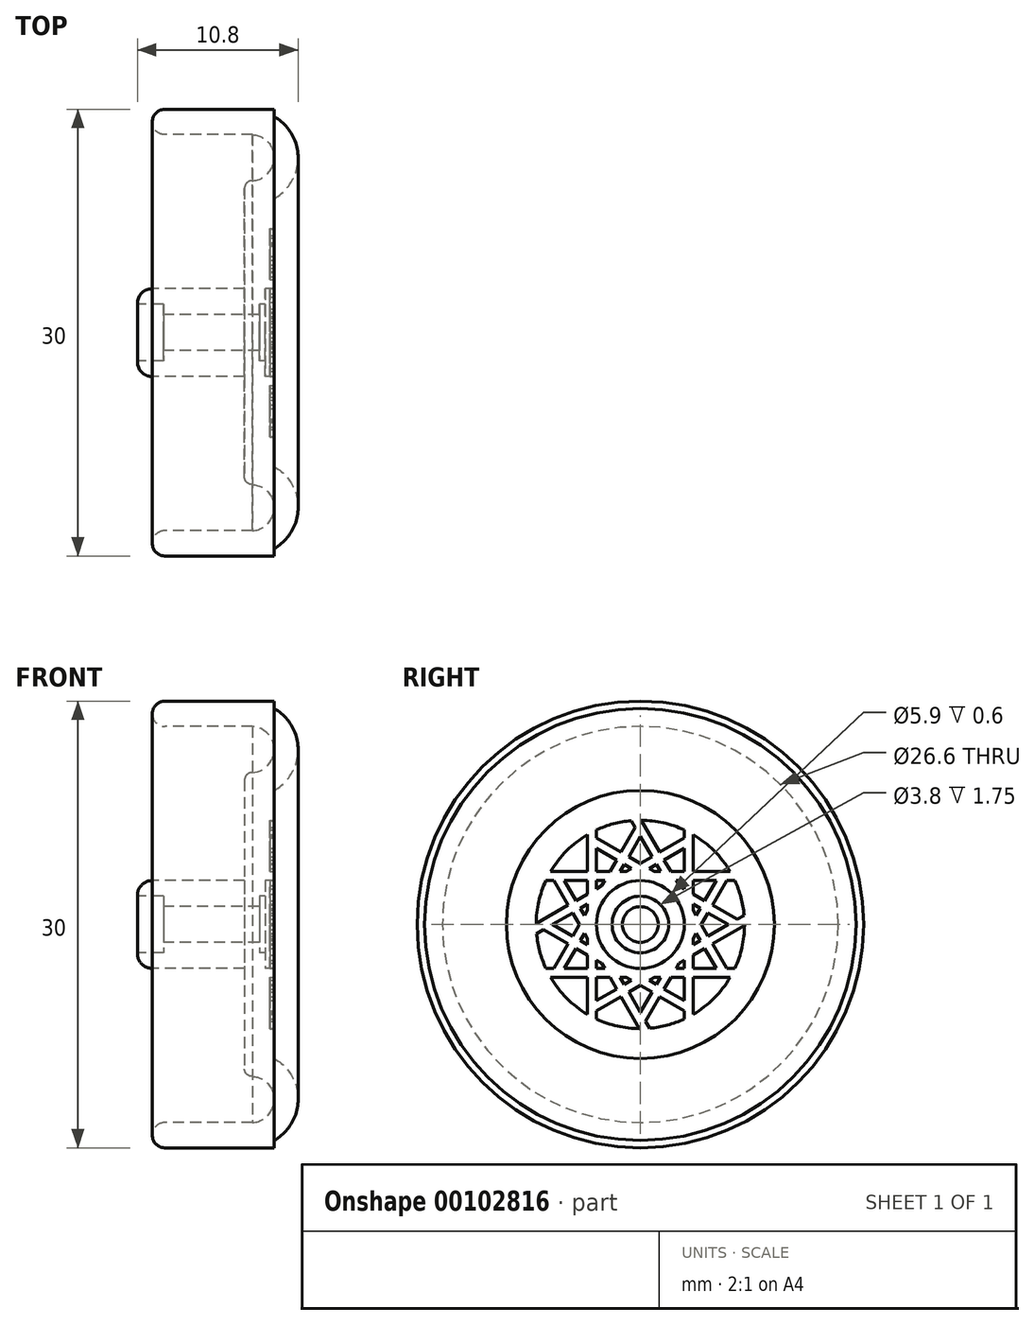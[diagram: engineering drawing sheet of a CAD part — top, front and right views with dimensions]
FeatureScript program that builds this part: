
annotation { "Feature Type Name" : "Feature", "Feature Type Description" : "" }
export const myFeature = defineFeature(function(context is Context, id is Id, definition is map)
    precondition{}
    {
        {
            var Q0;
            Q0=qCreatedBy(makeId("Top.planeOp"),FACE);
            var sketch = newSketch(context, id + "F0", { "sketchPlane" : qUnion([Q0])});
            skLineSegment(sketch, "E0.bottom", {"start": v(4.9, 15) * mm, "end": v(-4.9, 15) * mm, "construction": true});
            skLineSegment(sketch, "E0.top", {"start": v(4.9, -15) * mm, "end": v(-4.9, -15) * mm, "construction": true});
            skLineSegment(sketch, "E0.left", {"start": v(4.9, 15) * mm, "end": v(4.9, -15) * mm, "construction": true});
            skPoint(sketch, "E0.middle", {"position": v(0, 0) * mm});
            skLineSegment(sketch, "E1", {"start": v(-4.05, 15) * mm, "end": v(3.3, 15) * mm});
            skLineSegment(sketch, "E2", {"start": v(3.3, 9) * mm, "end": v(3.3, 2.95) * mm});
            skLineSegment(sketch, "E3", {"start": v(2.3, 1.2) * mm, "end": v(-4.15, 1.2) * mm});
            skLineSegment(sketch, "E4", {"start": v(-4.15, 1.2) * mm, "end": v(-4.15, 1.9) * mm});
            skLineSegment(sketch, "E5", {"start": v(-4.15, 1.9) * mm, "end": v(-5.9, 1.9) * mm});
            skLineSegment(sketch, "E6.0", {"start": v(-4.05, 13.3) * mm, "end": v(1.84, 13.3) * mm});
            skLineSegment(sketch, "E7.0", {"start": v(1.3, 9.7) * mm, "end": v(1.3, 2.95) * mm});
            skLineSegment(sketch, "E8.0", {"start": v(1.3, 2.95) * mm, "end": v(-4.9, 2.95) * mm});
            skArc(sketch, "E9", {"start": v(-4.05, 15) * mm, "mid": v(-4.9, 14.15) * mm, "end": v(-4.05, 13.3) * mm});
            skLineSegment(sketch, "E10", {"start": v(2.3, 1.2) * mm, "end": v(2.3, 1.9) * mm});
            skLineSegment(sketch, "E11", {"start": v(2.3, 1.9) * mm, "end": v(2.7, 1.9) * mm});
            skLineSegment(sketch, "E12", {"start": v(2.7, 1.9) * mm, "end": v(2.7, 2.95) * mm});
            skLineSegment(sketch, "E13", {"start": v(2.7, 2.95) * mm, "end": v(3.3, 2.95) * mm});
            skLineSegment(sketch, "E14", {"start": v(-5.9, 1.95) * mm, "end": v(-5.9, 1.9) * mm});
            skLineSegment(sketch, "E15", {"start": v(-5, 0) * mm, "end": v(4.9, 0) * mm, "construction": true});
            skPoint(sketch, "E16.visualSharp", {"position": v(-5.9, 2.95) * mm});
            skArc(sketch, "E16.filletArc", {"start": v(-4.9, 2.95) * mm, "mid": v(-5.6, 2.66) * mm, "end": v(-5.9, 1.95) * mm});
            skLineSegment(sketch, "E17", {"start": v(1.23, 0) * mm, "end": v(1.23, 17.38) * mm, "construction": true});
            skLineSegment(sketch, "E18", {"start": v(3.3, 15) * mm, "end": v(3.3, 14.5) * mm});
            skArc(sketch, "E19", {"start": v(3.3, 9) * mm, "mid": v(4.9, 11.75) * mm, "end": v(3.3, 14.5) * mm});
            skLineSegment(sketch, "E20", {"start": v(-4.9, 15) * mm, "end": v(-4.9, 12.83) * mm, "construction": true});
            skArc(sketch, "E21", {"start": v(1.78, 10.2) * mm, "mid": v(3.29, 11.72) * mm, "end": v(1.84, 13.3) * mm});
            skPoint(sketch, "E22.visualSharp", {"position": v(1.3, 10.26) * mm});
            skArc(sketch, "E22.filletArc", {"start": v(1.78, 10.2) * mm, "mid": v(1.44, 10.05) * mm, "end": v(1.3, 9.7) * mm});
            skSolve(sketch);
        }
        {
            var Q0;
            Q0=makeQuery(id+"F0.imprint","IMPRINT",FACE,{"disambiguationData":[TD([[makeQuery(id+"F0.imprint","IMPRINT",EDGE,{"derivedFrom":sQuery(id+"F0.wireOp",EDGE,"E1")}),-1.0]])]});
            var Q1;
            Q1=sQuery(id+"F0.wireOp",EDGE,"E15");
            revolve(context, id + "F1", {"entities" : qUnion([Q0]), "axis" : qUnion([Q1]), "revolveType" : RevolveType.FULL});
        }
        {
            var Q0;
            Q0=makeQuery(id+"F1.opRevolve","SWEPT_FACE",FACE,{"disambiguationData":[OSD([sQuery(id+"F0.wireOp",EDGE,"E2")])]});
            var sketch = newSketch(context, id + "F2", { "sketchPlane" : qUnion([Q0])});
            skCircle(sketch, "E23", {"center": v(0, 0) * mm, "radius": 7 * mm});
            skLineSegment(sketch, "E24", {"start": v(2.95, 6.35) * mm, "end": v(2.95, -6.35) * mm});
            skLineSegment(sketch, "E25.0", {"start": v(3.55, 6.03) * mm, "end": v(3.55, -6.03) * mm});
            skLineSegment(sketch, "E26.1.0", {"start": v(-3.55, -6.03) * mm, "end": v(-3.55, 6.03) * mm});
            skLineSegment(sketch, "E26.1.1", {"start": v(-2.95, -6.35) * mm, "end": v(-2.95, 6.35) * mm});
            skLineSegment(sketch, "E27.1.0", {"start": v(6.35, -2.95) * mm, "end": v(-6.35, -2.95) * mm});
            skLineSegment(sketch, "E27.1.1", {"start": v(6.03, -3.55) * mm, "end": v(-6.03, -3.55) * mm});
            skLineSegment(sketch, "E27.1.2", {"start": v(-6.03, 3.55) * mm, "end": v(6.03, 3.55) * mm});
            skLineSegment(sketch, "E27.1.3", {"start": v(-6.35, 2.95) * mm, "end": v(6.35, 2.95) * mm});
            skLineSegment(sketch, "E28.1.0", {"start": v(6.97, 0.62) * mm, "end": v(-4.02, -5.73) * mm});
            skLineSegment(sketch, "E28.1.1", {"start": v(7, -0.06) * mm, "end": v(-3.45, -6.1) * mm});
            skLineSegment(sketch, "E28.1.2", {"start": v(-0.06, -7) * mm, "end": v(-6.1, 3.45) * mm});
            skLineSegment(sketch, "E28.1.3", {"start": v(0.62, -6.97) * mm, "end": v(-5.73, 4.02) * mm});
            skLineSegment(sketch, "E28.1.4", {"start": v(-0.62, 6.97) * mm, "end": v(5.73, -4.02) * mm});
            skLineSegment(sketch, "E28.1.5", {"start": v(0.06, 7) * mm, "end": v(6.1, -3.45) * mm});
            skLineSegment(sketch, "E28.1.6", {"start": v(-6.97, -0.62) * mm, "end": v(4.02, 5.73) * mm});
            skLineSegment(sketch, "E28.1.7", {"start": v(-7, 0.06) * mm, "end": v(3.45, 6.1) * mm});
            skLineSegment(sketch, "E28.2.0", {"start": v(-4.02, 5.73) * mm, "end": v(6.97, -0.62) * mm});
            skLineSegment(sketch, "E28.2.1", {"start": v(-3.45, 6.1) * mm, "end": v(7, 0.06) * mm});
            skLineSegment(sketch, "E28.2.2", {"start": v(6.1, 3.45) * mm, "end": v(0.06, -7) * mm});
            skLineSegment(sketch, "E28.2.3", {"start": v(5.73, 4.02) * mm, "end": v(-0.62, -6.97) * mm});
            skLineSegment(sketch, "E28.2.4", {"start": v(-5.73, -4.02) * mm, "end": v(0.62, 6.97) * mm});
            skLineSegment(sketch, "E28.2.5", {"start": v(-6.1, -3.45) * mm, "end": v(-0.06, 7) * mm});
            skLineSegment(sketch, "E28.2.6", {"start": v(4.02, -5.73) * mm, "end": v(-6.97, 0.62) * mm});
            skLineSegment(sketch, "E28.2.7", {"start": v(3.45, -6.1) * mm, "end": v(-7, -0.06) * mm});
            skSolve(sketch);
        }
        {
            var Q0;
            {var subQ0=sQuery(id+"F2.wireOp",EDGE,"E28.1.3");var subQ1=sQuery(id+"F2.wireOp",EDGE,"E23");var subQ2=makeQuery(id+"F2.imprint","INTERSECT",VERTEX,{"disambiguationData":[OD(1.0)],"derivedFrom":[subQ1,subQ0]});Q0=makeQuery(id+"F2.imprint","IMPRINT",FACE,{"disambiguationData":[TD([[makeQuery(id+"F2.imprint","IMPRINT",EDGE,{"disambiguationData":[TD([[subQ2,1.0]])],"derivedFrom":subQ1}),1.0]])]});}
            var Q1;
            {var subQ0=sQuery(id+"F2.wireOp",EDGE,"E26.1.0");var subQ1=sQuery(id+"F2.wireOp",EDGE,"E23");var subQ2=makeQuery(id+"F2.imprint","INTERSECT",VERTEX,{"disambiguationData":[OD(1.0)],"derivedFrom":[subQ1,subQ0]});Q1=makeQuery(id+"F2.imprint","IMPRINT",FACE,{"disambiguationData":[TD([[makeQuery(id+"F2.imprint","IMPRINT",EDGE,{"disambiguationData":[TD([[subQ2,-1.0]])],"derivedFrom":subQ1}),1.0]])]});}
            var Q2;
            {var subQ0=sQuery(id+"F2.wireOp",EDGE,"E27.1.2");var subQ1=sQuery(id+"F2.wireOp",EDGE,"E26.1.1");var subQ2=makeQuery(id+"F2.imprint","INTERSECT",VERTEX,{"derivedFrom":[subQ1,subQ0]});Q2=makeQuery(id+"F2.imprint","IMPRINT",FACE,{"disambiguationData":[TD([[makeQuery(id+"F2.imprint","IMPRINT",EDGE,{"disambiguationData":[TD([[subQ2,-1.0]])],"derivedFrom":subQ1}),-1.0]])]});}
            var Q3;
            {var subQ1=sQuery(id+"F2.wireOp",EDGE,"E23");var subQ5=sQuery(id+"F2.wireOp",EDGE,"E26.1.1");var subQ6=makeQuery(id+"F2.imprint","INTERSECT",VERTEX,{"disambiguationData":[OD(1.0)],"derivedFrom":[subQ1,subQ5]});Q3=makeQuery(id+"F2.imprint","IMPRINT",FACE,{"disambiguationData":[TD([[makeQuery(id+"F2.imprint","IMPRINT",EDGE,{"disambiguationData":[TD([[subQ6,1.0]])],"derivedFrom":subQ1}),1.0]])]});}
            var Q4;
            {var subQ0=sQuery(id+"F2.wireOp",EDGE,"E28.1.5");var subQ1=sQuery(id+"F2.wireOp",EDGE,"E23");var subQ2=makeQuery(id+"F2.imprint","INTERSECT",VERTEX,{"disambiguationData":[OD(0.0)],"derivedFrom":[subQ1,subQ0]});Q4=makeQuery(id+"F2.imprint","IMPRINT",FACE,{"disambiguationData":[TD([[makeQuery(id+"F2.imprint","IMPRINT",EDGE,{"disambiguationData":[TD([[subQ2,1.0]])],"derivedFrom":subQ1}),1.0]])]});}
            var Q5;
            {var subQ1=sQuery(id+"F2.wireOp",EDGE,"E24");var subQ7=sQuery(id+"F2.wireOp",EDGE,"E23");var subQ8=makeQuery(id+"F2.imprint","INTERSECT",VERTEX,{"disambiguationData":[OD(0.0)],"derivedFrom":[subQ7,subQ1]});Q5=makeQuery(id+"F2.imprint","IMPRINT",FACE,{"disambiguationData":[TD([[makeQuery(id+"F2.imprint","IMPRINT",EDGE,{"disambiguationData":[TD([[subQ8,-1.0]])],"derivedFrom":subQ7}),1.0]])]});}
            var Q6;
            {var subQ0=sQuery(id+"F2.wireOp",EDGE,"E28.2.4");var subQ1=sQuery(id+"F2.wireOp",EDGE,"E28.1.4");var subQ2=makeQuery(id+"F2.imprint","INTERSECT",VERTEX,{"derivedFrom":[subQ1,subQ0]});Q6=makeQuery(id+"F2.imprint","IMPRINT",FACE,{"disambiguationData":[TD([[makeQuery(id+"F2.imprint","IMPRINT",EDGE,{"disambiguationData":[TD([[subQ2,-1.0]])],"derivedFrom":subQ1}),-1.0]])]});}
            var Q7;
            {var subQ0=sQuery(id+"F2.wireOp",EDGE,"E28.2.4");var subQ1=sQuery(id+"F2.wireOp",EDGE,"E27.1.2");var subQ2=makeQuery(id+"F2.imprint","INTERSECT",VERTEX,{"derivedFrom":[subQ1,subQ0]});Q7=makeQuery(id+"F2.imprint","IMPRINT",FACE,{"disambiguationData":[TD([[makeQuery(id+"F2.imprint","IMPRINT",EDGE,{"disambiguationData":[TD([[subQ2,-1.0]])],"derivedFrom":subQ1}),1.0]])]});}
            var Q8;
            {var subQ0=sQuery(id+"F2.wireOp",EDGE,"E28.2.1");var subQ1=sQuery(id+"F2.wireOp",EDGE,"E27.1.2");var subQ2=makeQuery(id+"F2.imprint","INTERSECT",VERTEX,{"derivedFrom":[subQ1,subQ0]});Q8=makeQuery(id+"F2.imprint","IMPRINT",FACE,{"disambiguationData":[TD([[makeQuery(id+"F2.imprint","IMPRINT",EDGE,{"disambiguationData":[TD([[subQ2,-1.0]])],"derivedFrom":subQ1}),1.0]])]});}
            var Q9;
            {var subQ0=sQuery(id+"F2.wireOp",EDGE,"E28.1.6");var subQ1=sQuery(id+"F2.wireOp",EDGE,"E24");var subQ2=makeQuery(id+"F2.imprint","INTERSECT",VERTEX,{"derivedFrom":[subQ1,subQ0]});Q9=makeQuery(id+"F2.imprint","IMPRINT",FACE,{"disambiguationData":[TD([[makeQuery(id+"F2.imprint","IMPRINT",EDGE,{"disambiguationData":[TD([[subQ2,-1.0]])],"derivedFrom":subQ1}),-1.0]])]});}
            var Q10;
            {var subQ0=sQuery(id+"F2.wireOp",EDGE,"E28.1.6");var subQ1=sQuery(id+"F2.wireOp",EDGE,"E23");var subQ2=makeQuery(id+"F2.imprint","INTERSECT",VERTEX,{"disambiguationData":[OD(1.0)],"derivedFrom":[subQ1,subQ0]});Q10=makeQuery(id+"F2.imprint","IMPRINT",FACE,{"disambiguationData":[TD([[makeQuery(id+"F2.imprint","IMPRINT",EDGE,{"disambiguationData":[TD([[subQ2,1.0]])],"derivedFrom":subQ1}),1.0]])]});}
            var Q11;
            {var subQ0=sQuery(id+"F2.wireOp",EDGE,"E27.1.3");var subQ1=sQuery(id+"F2.wireOp",EDGE,"E24");var subQ2=makeQuery(id+"F2.imprint","INTERSECT",VERTEX,{"derivedFrom":[subQ1,subQ0]});Q11=makeQuery(id+"F2.imprint","IMPRINT",FACE,{"disambiguationData":[TD([[makeQuery(id+"F2.imprint","IMPRINT",EDGE,{"disambiguationData":[TD([[subQ2,-1.0]])],"derivedFrom":subQ1}),-1.0]])]});}
            var Q12;
            {var subQ0=sQuery(id+"F2.wireOp",EDGE,"E27.1.3");var subQ1=sQuery(id+"F2.wireOp",EDGE,"E25.0");var subQ2=makeQuery(id+"F2.imprint","INTERSECT",VERTEX,{"derivedFrom":[subQ1,subQ0]});Q12=makeQuery(id+"F2.imprint","IMPRINT",FACE,{"disambiguationData":[TD([[makeQuery(id+"F2.imprint","IMPRINT",EDGE,{"disambiguationData":[TD([[subQ2,-1.0]])],"derivedFrom":subQ1}),1.0]])]});}
            var Q13;
            {var subQ5=sQuery(id+"F2.wireOp",EDGE,"E27.1.3");var subQ6=sQuery(id+"F2.wireOp",EDGE,"E23");var subQ7=makeQuery(id+"F2.imprint","INTERSECT",VERTEX,{"disambiguationData":[OD(1.0)],"derivedFrom":[subQ6,subQ5]});Q13=makeQuery(id+"F2.imprint","IMPRINT",FACE,{"disambiguationData":[TD([[makeQuery(id+"F2.imprint","IMPRINT",EDGE,{"disambiguationData":[TD([[subQ7,1.0]])],"derivedFrom":subQ6}),1.0]])]});}
            var Q14;
            {var subQ0=sQuery(id+"F2.wireOp",EDGE,"E28.2.0");var subQ1=sQuery(id+"F2.wireOp",EDGE,"E25.0");var subQ2=makeQuery(id+"F2.imprint","INTERSECT",VERTEX,{"derivedFrom":[subQ1,subQ0]});Q14=makeQuery(id+"F2.imprint","IMPRINT",FACE,{"disambiguationData":[TD([[makeQuery(id+"F2.imprint","IMPRINT",EDGE,{"disambiguationData":[TD([[subQ2,-1.0]])],"derivedFrom":subQ1}),1.0]])]});}
            var Q15;
            {var subQ0=sQuery(id+"F2.wireOp",EDGE,"E28.2.0");var subQ1=sQuery(id+"F2.wireOp",EDGE,"E28.1.0");var subQ2=makeQuery(id+"F2.imprint","INTERSECT",VERTEX,{"derivedFrom":[subQ1,subQ0]});Q15=makeQuery(id+"F2.imprint","IMPRINT",FACE,{"disambiguationData":[TD([[makeQuery(id+"F2.imprint","IMPRINT",EDGE,{"disambiguationData":[TD([[subQ2,-1.0]])],"derivedFrom":subQ1}),-1.0]])]});}
            var Q16;
            {var subQ5=sQuery(id+"F2.wireOp",EDGE,"E27.1.0");var subQ6=sQuery(id+"F2.wireOp",EDGE,"E23");var subQ7=makeQuery(id+"F2.imprint","INTERSECT",VERTEX,{"disambiguationData":[OD(0.0)],"derivedFrom":[subQ6,subQ5]});Q16=makeQuery(id+"F2.imprint","IMPRINT",FACE,{"disambiguationData":[TD([[makeQuery(id+"F2.imprint","IMPRINT",EDGE,{"disambiguationData":[TD([[subQ7,-1.0]])],"derivedFrom":subQ6}),1.0]])]});}
            var Q17;
            {var subQ0=sQuery(id+"F2.wireOp",EDGE,"E28.2.2");var subQ1=sQuery(id+"F2.wireOp",EDGE,"E25.0");var subQ2=makeQuery(id+"F2.imprint","INTERSECT",VERTEX,{"derivedFrom":[subQ1,subQ0]});Q17=makeQuery(id+"F2.imprint","IMPRINT",FACE,{"disambiguationData":[TD([[makeQuery(id+"F2.imprint","IMPRINT",EDGE,{"disambiguationData":[TD([[subQ2,-1.0]])],"derivedFrom":subQ1}),1.0]])]});}
            var Q18;
            {var subQ0=sQuery(id+"F2.wireOp",EDGE,"E28.1.1");var subQ1=sQuery(id+"F2.wireOp",EDGE,"E25.0");var subQ2=makeQuery(id+"F2.imprint","INTERSECT",VERTEX,{"derivedFrom":[subQ1,subQ0]});Q18=makeQuery(id+"F2.imprint","IMPRINT",FACE,{"disambiguationData":[TD([[makeQuery(id+"F2.imprint","IMPRINT",EDGE,{"disambiguationData":[TD([[subQ2,-1.0]])],"derivedFrom":subQ1}),1.0]])]});}
            var Q19;
            {var subQ0=sQuery(id+"F2.wireOp",EDGE,"E28.1.1");var subQ1=sQuery(id+"F2.wireOp",EDGE,"E24");var subQ2=makeQuery(id+"F2.imprint","INTERSECT",VERTEX,{"derivedFrom":[subQ1,subQ0]});Q19=makeQuery(id+"F2.imprint","IMPRINT",FACE,{"disambiguationData":[TD([[makeQuery(id+"F2.imprint","IMPRINT",EDGE,{"disambiguationData":[TD([[subQ2,-1.0]])],"derivedFrom":subQ1}),-1.0]])]});}
            var Q20;
            {var subQ0=sQuery(id+"F2.wireOp",EDGE,"E27.1.1");var subQ1=sQuery(id+"F2.wireOp",EDGE,"E24");var subQ2=makeQuery(id+"F2.imprint","INTERSECT",VERTEX,{"derivedFrom":[subQ1,subQ0]});Q20=makeQuery(id+"F2.imprint","IMPRINT",FACE,{"disambiguationData":[TD([[makeQuery(id+"F2.imprint","IMPRINT",EDGE,{"disambiguationData":[TD([[subQ2,-1.0]])],"derivedFrom":subQ1}),-1.0]])]});}
            var Q21;
            {var subQ3=sQuery(id+"F2.wireOp",EDGE,"E28.1.4");var subQ5=sQuery(id+"F2.wireOp",EDGE,"E23");var subQ6=makeQuery(id+"F2.imprint","INTERSECT",VERTEX,{"disambiguationData":[OD(1.0)],"derivedFrom":[subQ5,subQ3]});Q21=makeQuery(id+"F2.imprint","IMPRINT",FACE,{"disambiguationData":[TD([[makeQuery(id+"F2.imprint","IMPRINT",EDGE,{"disambiguationData":[TD([[subQ6,1.0]])],"derivedFrom":subQ5}),1.0]])]});}
            var Q22;
            {var subQ0=sQuery(id+"F2.wireOp",EDGE,"E28.2.3");var subQ1=sQuery(id+"F2.wireOp",EDGE,"E27.1.1");var subQ2=makeQuery(id+"F2.imprint","INTERSECT",VERTEX,{"derivedFrom":[subQ1,subQ0]});Q22=makeQuery(id+"F2.imprint","IMPRINT",FACE,{"disambiguationData":[TD([[makeQuery(id+"F2.imprint","IMPRINT",EDGE,{"disambiguationData":[TD([[subQ2,-1.0]])],"derivedFrom":subQ1}),1.0]])]});}
            var Q23;
            {var subQ5=sQuery(id+"F2.wireOp",EDGE,"E23");var subQ7=sQuery(id+"F2.wireOp",EDGE,"E24");var subQ8=makeQuery(id+"F2.imprint","INTERSECT",VERTEX,{"disambiguationData":[OD(1.0)],"derivedFrom":[subQ5,subQ7]});Q23=makeQuery(id+"F2.imprint","IMPRINT",FACE,{"disambiguationData":[TD([[makeQuery(id+"F2.imprint","IMPRINT",EDGE,{"disambiguationData":[TD([[subQ8,1.0]])],"derivedFrom":subQ5}),1.0]])]});}
            var Q24;
            {var subQ0=sQuery(id+"F2.wireOp",EDGE,"E25.0");var subQ1=sQuery(id+"F2.wireOp",EDGE,"E23");var subQ2=makeQuery(id+"F2.imprint","INTERSECT",VERTEX,{"disambiguationData":[OD(1.0)],"derivedFrom":[subQ1,subQ0]});Q24=makeQuery(id+"F2.imprint","IMPRINT",FACE,{"disambiguationData":[TD([[makeQuery(id+"F2.imprint","IMPRINT",EDGE,{"disambiguationData":[TD([[subQ2,-1.0]])],"derivedFrom":subQ1}),1.0]])]});}
            var Q25;
            {var subQ0=sQuery(id+"F2.wireOp",EDGE,"E27.1.1");var subQ1=sQuery(id+"F2.wireOp",EDGE,"E23");var subQ2=makeQuery(id+"F2.imprint","INTERSECT",VERTEX,{"disambiguationData":[OD(0.0)],"derivedFrom":[subQ1,subQ0]});Q25=makeQuery(id+"F2.imprint","IMPRINT",FACE,{"disambiguationData":[TD([[makeQuery(id+"F2.imprint","IMPRINT",EDGE,{"disambiguationData":[TD([[subQ2,1.0]])],"derivedFrom":subQ1}),1.0]])]});}
            var Q26;
            {var subQ0=sQuery(id+"F2.wireOp",EDGE,"E28.1.1");var subQ1=sQuery(id+"F2.wireOp",EDGE,"E23");var subQ2=makeQuery(id+"F2.imprint","INTERSECT",VERTEX,{"disambiguationData":[OD(0.0)],"derivedFrom":[subQ1,subQ0]});Q26=makeQuery(id+"F2.imprint","IMPRINT",FACE,{"disambiguationData":[TD([[makeQuery(id+"F2.imprint","IMPRINT",EDGE,{"disambiguationData":[TD([[subQ2,1.0]])],"derivedFrom":subQ1}),1.0]])]});}
            var Q27;
            {var subQ0=sQuery(id+"F2.wireOp",EDGE,"E27.1.2");var subQ1=sQuery(id+"F2.wireOp",EDGE,"E23");var subQ2=makeQuery(id+"F2.imprint","INTERSECT",VERTEX,{"disambiguationData":[OD(1.0)],"derivedFrom":[subQ1,subQ0]});Q27=makeQuery(id+"F2.imprint","IMPRINT",FACE,{"disambiguationData":[TD([[makeQuery(id+"F2.imprint","IMPRINT",EDGE,{"disambiguationData":[TD([[subQ2,-1.0]])],"derivedFrom":subQ1}),1.0]])]});}
            var Q28;
            {var subQ0=sQuery(id+"F2.wireOp",EDGE,"E25.0");var subQ1=sQuery(id+"F2.wireOp",EDGE,"E23");var subQ2=makeQuery(id+"F2.imprint","INTERSECT",VERTEX,{"disambiguationData":[OD(0.0)],"derivedFrom":[subQ1,subQ0]});Q28=makeQuery(id+"F2.imprint","IMPRINT",FACE,{"disambiguationData":[TD([[makeQuery(id+"F2.imprint","IMPRINT",EDGE,{"disambiguationData":[TD([[subQ2,1.0]])],"derivedFrom":subQ1}),1.0]])]});}
            var Q29;
            {var subQ0=sQuery(id+"F2.wireOp",EDGE,"E27.1.2");var subQ1=sQuery(id+"F2.wireOp",EDGE,"E23");var subQ2=makeQuery(id+"F2.imprint","INTERSECT",VERTEX,{"disambiguationData":[OD(0.0)],"derivedFrom":[subQ1,subQ0]});Q29=makeQuery(id+"F2.imprint","IMPRINT",FACE,{"disambiguationData":[TD([[makeQuery(id+"F2.imprint","IMPRINT",EDGE,{"disambiguationData":[TD([[subQ2,1.0]])],"derivedFrom":subQ1}),1.0]])]});}
            var Q30;
            {var subQ0=sQuery(id+"F2.wireOp",EDGE,"E28.1.7");var subQ1=sQuery(id+"F2.wireOp",EDGE,"E26.1.0");var subQ2=makeQuery(id+"F2.imprint","INTERSECT",VERTEX,{"derivedFrom":[subQ1,subQ0]});Q30=makeQuery(id+"F2.imprint","IMPRINT",FACE,{"disambiguationData":[TD([[makeQuery(id+"F2.imprint","IMPRINT",EDGE,{"disambiguationData":[TD([[subQ2,-1.0]])],"derivedFrom":subQ1}),1.0]])]});}
            var Q31;
            {var subQ0=sQuery(id+"F2.wireOp",EDGE,"E28.1.7");var subQ1=sQuery(id+"F2.wireOp",EDGE,"E26.1.1");var subQ2=makeQuery(id+"F2.imprint","INTERSECT",VERTEX,{"derivedFrom":[subQ1,subQ0]});Q31=makeQuery(id+"F2.imprint","IMPRINT",FACE,{"disambiguationData":[TD([[makeQuery(id+"F2.imprint","IMPRINT",EDGE,{"disambiguationData":[TD([[subQ2,-1.0]])],"derivedFrom":subQ1}),-1.0]])]});}
            var Q32;
            {var subQ5=sQuery(id+"F2.wireOp",EDGE,"E23");var subQ7=sQuery(id+"F2.wireOp",EDGE,"E27.1.3");var subQ9=makeQuery(id+"F2.imprint","INTERSECT",VERTEX,{"disambiguationData":[OD(0.0)],"derivedFrom":[subQ5,subQ7]});Q32=makeQuery(id+"F2.imprint","IMPRINT",FACE,{"disambiguationData":[TD([[makeQuery(id+"F2.imprint","IMPRINT",EDGE,{"disambiguationData":[TD([[subQ9,-1.0]])],"derivedFrom":subQ5}),1.0]])]});}
            var Q33;
            {var subQ0=sQuery(id+"F2.wireOp",EDGE,"E28.2.5");var subQ1=sQuery(id+"F2.wireOp",EDGE,"E26.1.0");var subQ2=makeQuery(id+"F2.imprint","INTERSECT",VERTEX,{"derivedFrom":[subQ1,subQ0]});Q33=makeQuery(id+"F2.imprint","IMPRINT",FACE,{"disambiguationData":[TD([[makeQuery(id+"F2.imprint","IMPRINT",EDGE,{"disambiguationData":[TD([[subQ2,-1.0]])],"derivedFrom":subQ1}),1.0]])]});}
            var Q34;
            {var subQ0=sQuery(id+"F2.wireOp",EDGE,"E28.1.7");var subQ1=sQuery(id+"F2.wireOp",EDGE,"E23");var subQ2=makeQuery(id+"F2.imprint","INTERSECT",VERTEX,{"disambiguationData":[OD(0.0)],"derivedFrom":[subQ1,subQ0]});Q34=makeQuery(id+"F2.imprint","IMPRINT",FACE,{"disambiguationData":[TD([[makeQuery(id+"F2.imprint","IMPRINT",EDGE,{"disambiguationData":[TD([[subQ2,1.0]])],"derivedFrom":subQ1}),1.0]])]});}
            var Q35;
            {var subQ0=sQuery(id+"F2.wireOp",EDGE,"E28.2.5");var subQ1=sQuery(id+"F2.wireOp",EDGE,"E28.1.2");var subQ2=makeQuery(id+"F2.imprint","INTERSECT",VERTEX,{"derivedFrom":[subQ1,subQ0]});Q35=makeQuery(id+"F2.imprint","IMPRINT",FACE,{"disambiguationData":[TD([[makeQuery(id+"F2.imprint","IMPRINT",EDGE,{"disambiguationData":[TD([[subQ2,-1.0]])],"derivedFrom":subQ1}),1.0]])]});}
            var Q36;
            {var subQ0=sQuery(id+"F2.wireOp",EDGE,"E28.2.6");var subQ1=sQuery(id+"F2.wireOp",EDGE,"E26.1.0");var subQ2=makeQuery(id+"F2.imprint","INTERSECT",VERTEX,{"derivedFrom":[subQ1,subQ0]});Q36=makeQuery(id+"F2.imprint","IMPRINT",FACE,{"disambiguationData":[TD([[makeQuery(id+"F2.imprint","IMPRINT",EDGE,{"disambiguationData":[TD([[subQ2,-1.0]])],"derivedFrom":subQ1}),1.0]])]});}
            var Q37;
            {var subQ1=sQuery(id+"F2.wireOp",EDGE,"E23");var subQ6=sQuery(id+"F2.wireOp",EDGE,"E27.1.0");var subQ9=makeQuery(id+"F2.imprint","INTERSECT",VERTEX,{"disambiguationData":[OD(1.0)],"derivedFrom":[subQ1,subQ6]});Q37=makeQuery(id+"F2.imprint","IMPRINT",FACE,{"disambiguationData":[TD([[makeQuery(id+"F2.imprint","IMPRINT",EDGE,{"disambiguationData":[TD([[subQ9,1.0]])],"derivedFrom":subQ1}),1.0]])]});}
            var Q38;
            {var subQ0=sQuery(id+"F2.wireOp",EDGE,"E27.1.0");var subQ1=sQuery(id+"F2.wireOp",EDGE,"E26.1.0");var subQ2=makeQuery(id+"F2.imprint","INTERSECT",VERTEX,{"derivedFrom":[subQ1,subQ0]});Q38=makeQuery(id+"F2.imprint","IMPRINT",FACE,{"disambiguationData":[TD([[makeQuery(id+"F2.imprint","IMPRINT",EDGE,{"disambiguationData":[TD([[subQ2,-1.0]])],"derivedFrom":subQ1}),1.0]])]});}
            var Q39;
            {var subQ0=sQuery(id+"F2.wireOp",EDGE,"E27.1.0");var subQ1=sQuery(id+"F2.wireOp",EDGE,"E26.1.1");var subQ2=makeQuery(id+"F2.imprint","INTERSECT",VERTEX,{"derivedFrom":[subQ1,subQ0]});Q39=makeQuery(id+"F2.imprint","IMPRINT",FACE,{"disambiguationData":[TD([[makeQuery(id+"F2.imprint","IMPRINT",EDGE,{"disambiguationData":[TD([[subQ2,-1.0]])],"derivedFrom":subQ1}),-1.0]])]});}
            var Q40;
            {var subQ0=sQuery(id+"F2.wireOp",EDGE,"E27.1.1");var subQ1=sQuery(id+"F2.wireOp",EDGE,"E23");var subQ2=makeQuery(id+"F2.imprint","INTERSECT",VERTEX,{"disambiguationData":[OD(1.0)],"derivedFrom":[subQ1,subQ0]});Q40=makeQuery(id+"F2.imprint","IMPRINT",FACE,{"disambiguationData":[TD([[makeQuery(id+"F2.imprint","IMPRINT",EDGE,{"disambiguationData":[TD([[subQ2,-1.0]])],"derivedFrom":subQ1}),1.0]])]});}
            var Q41;
            {var subQ0=sQuery(id+"F2.wireOp",EDGE,"E28.1.0");var subQ1=sQuery(id+"F2.wireOp",EDGE,"E23");var subQ2=makeQuery(id+"F2.imprint","INTERSECT",VERTEX,{"disambiguationData":[OD(1.0)],"derivedFrom":[subQ1,subQ0]});Q41=makeQuery(id+"F2.imprint","IMPRINT",FACE,{"disambiguationData":[TD([[makeQuery(id+"F2.imprint","IMPRINT",EDGE,{"disambiguationData":[TD([[subQ2,1.0]])],"derivedFrom":subQ1}),1.0]])]});}
            var Q42;
            {var subQ0=sQuery(id+"F2.wireOp",EDGE,"E26.1.0");var subQ1=sQuery(id+"F2.wireOp",EDGE,"E23");var subQ2=makeQuery(id+"F2.imprint","INTERSECT",VERTEX,{"disambiguationData":[OD(0.0)],"derivedFrom":[subQ1,subQ0]});Q42=makeQuery(id+"F2.imprint","IMPRINT",FACE,{"disambiguationData":[TD([[makeQuery(id+"F2.imprint","IMPRINT",EDGE,{"disambiguationData":[TD([[subQ2,1.0]])],"derivedFrom":subQ1}),1.0]])]});}
            var Q43;
            {var subQ0=sQuery(id+"F2.wireOp",EDGE,"E28.1.0");var subQ1=sQuery(id+"F2.wireOp",EDGE,"E26.1.1");var subQ2=makeQuery(id+"F2.imprint","INTERSECT",VERTEX,{"derivedFrom":[subQ1,subQ0]});Q43=makeQuery(id+"F2.imprint","IMPRINT",FACE,{"disambiguationData":[TD([[makeQuery(id+"F2.imprint","IMPRINT",EDGE,{"disambiguationData":[TD([[subQ2,-1.0]])],"derivedFrom":subQ1}),-1.0]])]});}
            var Q44;
            {var subQ0=sQuery(id+"F2.wireOp",EDGE,"E28.2.7");var subQ1=sQuery(id+"F2.wireOp",EDGE,"E27.1.1");var subQ2=makeQuery(id+"F2.imprint","INTERSECT",VERTEX,{"derivedFrom":[subQ1,subQ0]});Q44=makeQuery(id+"F2.imprint","IMPRINT",FACE,{"disambiguationData":[TD([[makeQuery(id+"F2.imprint","IMPRINT",EDGE,{"disambiguationData":[TD([[subQ2,-1.0]])],"derivedFrom":subQ1}),1.0]])]});}
            var Q45;
            {var subQ5=sQuery(id+"F2.wireOp",EDGE,"E26.1.1");var subQ6=sQuery(id+"F2.wireOp",EDGE,"E23");var subQ7=makeQuery(id+"F2.imprint","INTERSECT",VERTEX,{"disambiguationData":[OD(0.0)],"derivedFrom":[subQ6,subQ5]});Q45=makeQuery(id+"F2.imprint","IMPRINT",FACE,{"disambiguationData":[TD([[makeQuery(id+"F2.imprint","IMPRINT",EDGE,{"disambiguationData":[TD([[subQ7,-1.0]])],"derivedFrom":subQ6}),1.0]])]});}
            var Q46;
            {var subQ0=sQuery(id+"F2.wireOp",EDGE,"E28.1.2");var subQ1=sQuery(id+"F2.wireOp",EDGE,"E23");var subQ2=makeQuery(id+"F2.imprint","INTERSECT",VERTEX,{"disambiguationData":[OD(0.0)],"derivedFrom":[subQ1,subQ0]});Q46=makeQuery(id+"F2.imprint","IMPRINT",FACE,{"disambiguationData":[TD([[makeQuery(id+"F2.imprint","IMPRINT",EDGE,{"disambiguationData":[TD([[subQ2,1.0]])],"derivedFrom":subQ1}),1.0]])]});}
            var Q47;
            {var subQ0=sQuery(id+"F2.wireOp",EDGE,"E28.2.7");var subQ1=sQuery(id+"F2.wireOp",EDGE,"E28.1.1");var subQ2=makeQuery(id+"F2.imprint","INTERSECT",VERTEX,{"derivedFrom":[subQ1,subQ0]});Q47=makeQuery(id+"F2.imprint","IMPRINT",FACE,{"disambiguationData":[TD([[makeQuery(id+"F2.imprint","IMPRINT",EDGE,{"disambiguationData":[TD([[subQ2,-1.0]])],"derivedFrom":subQ1}),1.0]])]});}
            extrude(context, id + "F3", {"entities" : qUnion([Q0, Q1, Q2, Q3, Q4, Q5, Q6, Q7, Q8, Q9, Q10, Q11, Q12, Q13, Q14, Q15, Q16, Q17, Q18, Q19, Q20, Q21, Q22, Q23, Q24, Q25, Q26, Q27, Q28, Q29, Q30, Q31, Q32, Q33, Q34, Q35, Q36, Q37, Q38, Q39, Q40, Q41, Q42, Q43, Q44, Q45, Q46, Q47]), "operationType" : NewBodyOperationType.REMOVE, "oppositeDirection" : true, "depth" : 0.3 * mm});
        }
    });
